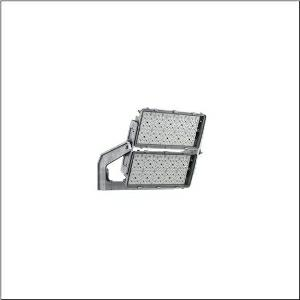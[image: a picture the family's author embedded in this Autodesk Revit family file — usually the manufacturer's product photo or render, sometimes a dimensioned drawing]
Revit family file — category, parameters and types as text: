
# Revit family: floodlight_fl_11_maxi_remote___rs12_5xa779514m01aa_cc46
name_source: partatom
category: Lighting Fixtures
units: mm (PartAtom-declared; Revit-internal decimal feet)

## family parameters
Cut with Voids When Loaded = No
Host = Face
Light Source = No
Part Type = Normal
Room Calculation Point = No
Round Connector Dimension = Use Diameter
Shared = No

## types (1)
- --- (1 x LED, 90180 lm, 916.8 W, 5700K)
    Apparent Load = 917 VA
    CIE Flux Codes = 79 92 99 100 100
    Color Rendering = 90
    Color Temperature = 5700K
    Default Elevation = 1800 mm
    Description = Floodlight FL 11  maxi  Remote floodlight; light control with lens of PMMA; cover panel of toughened safety glass, transparent; light distribution: RS12, rotationally symmetric direct distribution, LEDcolour temperature: 5700K, rated luminous flux: 90.180lm, colour rendering: CRI > 90, light colour: 957; luminous efficacy: 98lm/W; brightness control: DMX+RDM; with terminal, 6-pole, max. 2.5mm², mains connection: 220..240V/380..400V AC, 50/60Hz, surge voltage resistance: line to ground: 10kV, ECG replaceable separately, no afterglow with DALI off / DMX off command, LED unit replaceable without ESD environment, dustproof LED module, dimming range 10..100%; 917W floodlight with 2x LED unit of diecast aluminium, coated grey; length: 713mm / width: 651mm / height: 338mm; housing frame, of diecast aluminium, uncoated, natural, mounting bracket, of diecast aluminium, uncoated, natural, equipment: Power, protection rating (complete): IP66; insulation class (complete): insulation class I (protective earthing); certification: CE, ENEC, VDE; ball protection: ball impact resistance with accessories, rated ambient temperature 10°C, only for outdoor installations, permissible operating ambient temperature: -40..+30°C, permissible storage temperature: -40..+85°C; packaging unit: 1 piece

Light Distribution: RS12
    Height = 320 mm
    Lamp = 1 x LED
    Lamp Light Flux = 90180 lm
    Lamp Power = 916.8 W
    Lamp count = 1
    Length = 712 mm
    Luminous efficacy = 98 lm/W
    Manufacturer = Siteco
    ModVariant = No
    Model = 5XA779514M01AA
    Number of Poles = 1
    OnlyDefault = Yes
    Power Factor = 1
    Product Name = Floodlight FL 11 maxi Remote | RS12
    Product group = floodlight | pylon top
    ProductGroupID = 6101
    Protection Class = Protection class I
    Protection Degree = IP 66
    RLX_Detail_Level = 1
    RlxData = <blob elided: 41125 chars, md5=e5e2eff7>
    Socket = socket
    Standby Power = 0 W
    System Light Flux = 90180 lm
    System Power = 917 W
    Type Comments = factory setting: luminous flux: 100 % | dim-lin: 254 | 950 mA
    Type Image = l_1006788.jpg
    URL = http://relux.com
    VarID = @adj_095691
    Voltage = 0 V
    Weight = 0.00 kg
    Width = 655 mm

## geometry (parser evidence)
native form markers: Blend x4, Sweep x12
no freeform markers — native parametric forms only
